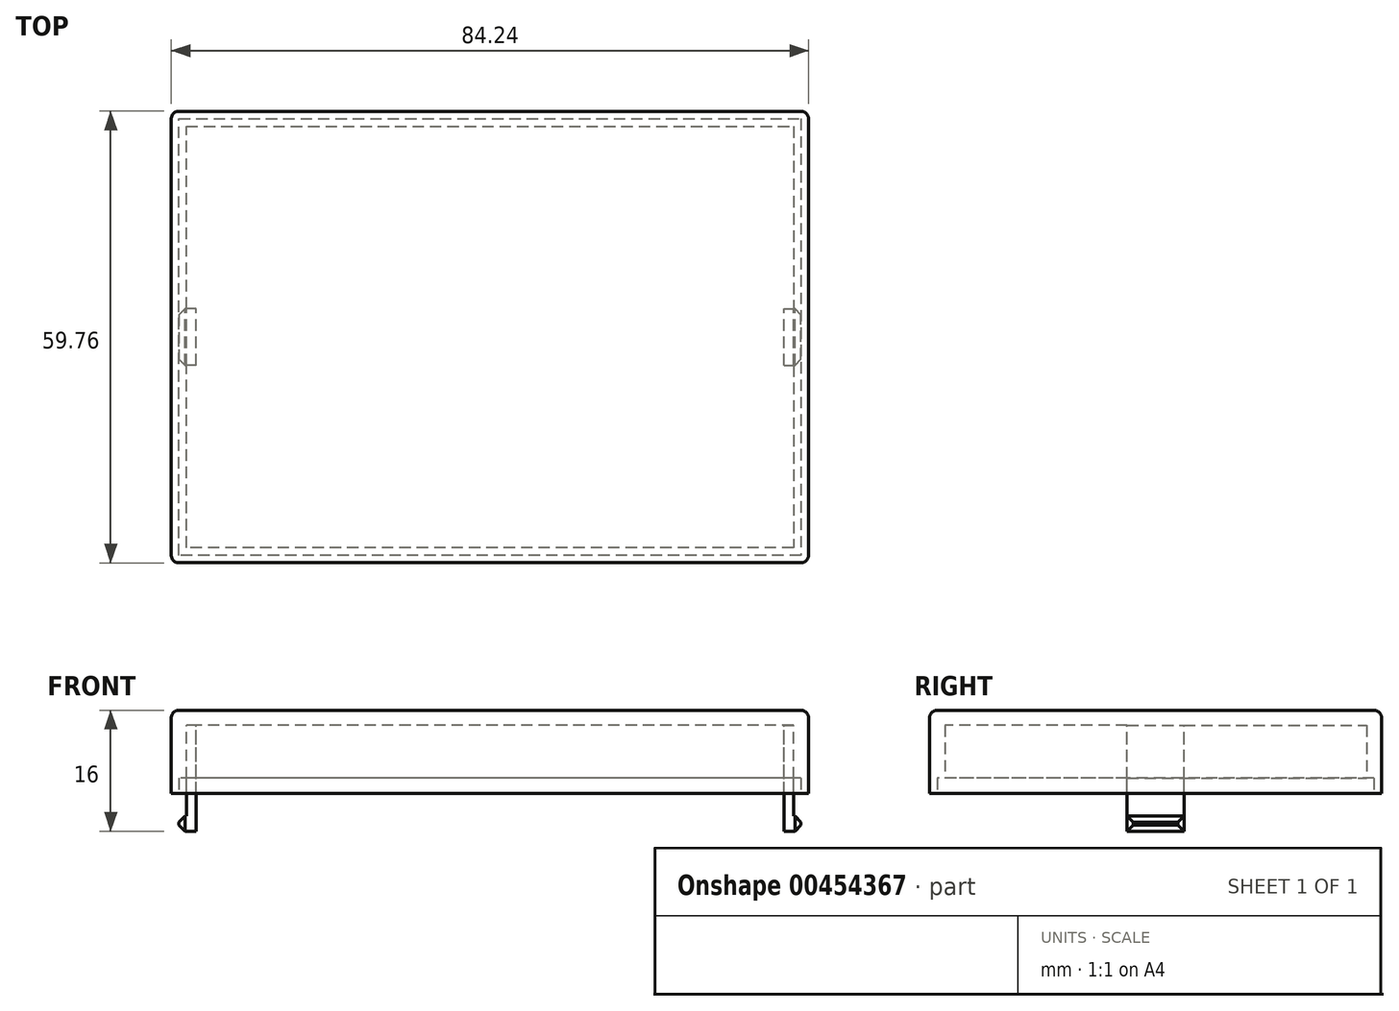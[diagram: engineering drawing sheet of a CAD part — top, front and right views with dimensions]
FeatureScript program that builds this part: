
annotation { "Feature Type Name" : "Feature", "Feature Type Description" : "" }
export const myFeature = defineFeature(function(context is Context, id is Id, definition is map)
    precondition{}
    {
        {
            var Q0;
            Q0=qCreatedBy(makeId("Top.planeOp"),FACE);
            var sketch = newSketch(context, id + "F0", { "sketchPlane" : qUnion([Q0])});
            skLineSegment(sketch, "E0.bottom", {"start": v(42.12, 29.88) * mm, "end": v(-42.12, 29.88) * mm});
            skLineSegment(sketch, "E0.top", {"start": v(42.13, -29.88) * mm, "end": v(-42.12, -29.88) * mm});
            skLineSegment(sketch, "E0.left", {"start": v(42.12, 29.88) * mm, "end": v(42.13, -29.88) * mm});
            skLineSegment(sketch, "E0.right", {"start": v(-42.12, 29.88) * mm, "end": v(-42.12, -29.88) * mm});
            skPoint(sketch, "E0.middle", {"position": v(0, 0) * mm});
            skSolve(sketch);
        }
        {
            var Q0;
            Q0=makeQuery(id+"F0.imprint","IMPRINT",FACE,{"disambiguationData":[TD([[makeQuery(id+"F0.imprint","IMPRINT",EDGE,{"derivedFrom":sQuery(id+"F0.wireOp",EDGE,"E0.bottom")}),1.0]])]});
            extrude(context, id + "F1", {"entities" : qUnion([Q0]), "depth" : 11 * mm});
        }
        {
            var Q0;
            Q0=makeQuery(id+"F1.opExtrude","CAP_FACE",FACE,{"disambiguationData":[OSD([sQuery(id+"F0.wireOp",EDGE,"E0.bottom"),sQuery(id+"F0.wireOp",EDGE,"E0.top"),sQuery(id+"F0.wireOp",EDGE,"E0.left"),sQuery(id+"F0.wireOp",EDGE,"E0.right")])],"isStart":true});
            var sketch = newSketch(context, id + "F2", { "sketchPlane" : qUnion([Q0])});
            skLineSegment(sketch, "E1.0", {"start": v(40.13, 27.88) * mm, "end": v(-40.12, 27.88) * mm});
            skLineSegment(sketch, "E1.1", {"start": v(40.12, -27.88) * mm, "end": v(40.13, 27.88) * mm});
            skLineSegment(sketch, "E1.2", {"start": v(-40.13, -27.88) * mm, "end": v(40.12, -27.88) * mm});
            skLineSegment(sketch, "E1.3", {"start": v(-40.12, 27.88) * mm, "end": v(-40.12, -27.88) * mm});
            skSolve(sketch);
        }
        {
            var Q0;
            Q0=makeQuery(id+"F2.imprint","IMPRINT",FACE,{"disambiguationData":[TD([[makeQuery(id+"F2.imprint","IMPRINT",EDGE,{"derivedFrom":sQuery(id+"F2.wireOp",EDGE,"E1.0")}),1.0]])]});
            extrude(context, id + "F3", {"entities" : qUnion([Q0]), "operationType" : NewBodyOperationType.REMOVE, "oppositeDirection" : true, "depth" : 9 * mm});
        }
        {
            var Q0;
            Q0=makeQuery(id+"F1.opExtrude","CAP_FACE",FACE,{"disambiguationData":[OSD([sQuery(id+"F0.wireOp",EDGE,"E0.bottom"),sQuery(id+"F0.wireOp",EDGE,"E0.top"),sQuery(id+"F0.wireOp",EDGE,"E0.left"),sQuery(id+"F0.wireOp",EDGE,"E0.right")])],"isStart":true});
            var sketch = newSketch(context, id + "F4", { "sketchPlane" : qUnion([Q0])});
            skLineSegment(sketch, "E2.0", {"start": v(41.13, 28.88) * mm, "end": v(-41.12, 28.88) * mm});
            skLineSegment(sketch, "E2.1", {"start": v(41.12, -28.88) * mm, "end": v(41.13, 28.88) * mm});
            skLineSegment(sketch, "E2.2", {"start": v(-41.12, -28.88) * mm, "end": v(41.12, -28.88) * mm});
            skLineSegment(sketch, "E2.3", {"start": v(-41.12, 28.88) * mm, "end": v(-41.12, -28.88) * mm});
            skSolve(sketch);
        }
        {
            var Q0;
            Q0=makeQuery(id+"F4.imprint","IMPRINT",FACE,{"disambiguationData":[TD([[makeQuery(id+"F4.imprint","IMPRINT",EDGE,{"derivedFrom":sQuery(id+"F4.wireOp",EDGE,"E2.0")}),1.0]])]});
            extrude(context, id + "F5", {"entities" : qUnion([Q0]), "operationType" : NewBodyOperationType.REMOVE, "oppositeDirection" : true, "depth" : 2 * mm});
        }
        {
            var Q0;
            Q0=makeQuery(id+"F3.boolean.opBoolean","COPY",FACE,{"derivedFrom":makeQuery(id+"F3.opExtrude","SWEPT_FACE",FACE,{"disambiguationData":[OSD([sQuery(id+"F2.wireOp",EDGE,"E1.3")])]})});
            var sketch = newSketch(context, id + "F6", { "sketchPlane" : qUnion([Q0])});
            skLineSegment(sketch, "E3.bottom", {"start": v(3.75, -5) * mm, "end": v(-3.75, -5) * mm});
            skLineSegment(sketch, "E3.top", {"start": v(3.75, 9) * mm, "end": v(-3.75, 9) * mm});
            skLineSegment(sketch, "E3.left", {"start": v(3.75, -5) * mm, "end": v(3.75, 9) * mm});
            skLineSegment(sketch, "E3.right", {"start": v(-3.75, -5) * mm, "end": v(-3.75, 9) * mm});
            skPoint(sketch, "E3.middle", {"position": v(0, 2) * mm});
            skSolve(sketch);
        }
        {
            var Q0;
            {var subQ0=sQuery(id+"F6.wireOp",EDGE,"E3.bottom");Q0=makeQuery(id+"F6.imprint","IMPRINT",FACE,{"disambiguationData":[TD([[makeQuery(id+"F6.imprint","IMPRINT",EDGE,{"derivedFrom":subQ0}),-1.0]])]});}
            var Q1;
            {var subQ0=sQuery(id+"F6.wireOp",EDGE,"E3.left");var subQ1=sQuery(id+"F2.wireOp",EDGE,"E1.3");var subQ2=makeQuery(id+"F5.boolean.opBoolean","COPY",EDGE,{"derivedFrom":makeQuery(id+"F5.opExtrude","CAP_EDGE",EDGE,{"disambiguationData":[OSD([subQ1])],"isStart":false})});var subQ3=makeQuery(id+"F6.imprint","INTERSECT",VERTEX,{"derivedFrom":[subQ2,subQ0]});Q1=makeQuery(id+"F6.imprint","IMPRINT",FACE,{"disambiguationData":[TD([[makeQuery(id+"F6.imprint","IMPRINT",EDGE,{"disambiguationData":[TD([[subQ3,-1.0]])],"derivedFrom":subQ0}),1.0]])]});}
            extrude(context, id + "F7", {"entities" : qUnion([Q0, Q1]), "operationType" : NewBodyOperationType.ADD, "depth" : 1.25 * mm});
        }
        {
            var Q0;
            Q0=makeQuery(id+"F1.opExtrude","SWEPT_EDGE",EDGE,{"disambiguationData":[OSD([sQuery(id+"F0.wireOp",EDGE,"E0.top"),sQuery(id+"F0.wireOp",EDGE,"E0.right")])]});
            var Q1;
            Q1=makeQuery(id+"F1.opExtrude","SWEPT_EDGE",EDGE,{"disambiguationData":[OSD([sQuery(id+"F0.wireOp",EDGE,"E0.top"),sQuery(id+"F0.wireOp",EDGE,"E0.left")])]});
            var Q2;
            Q2=makeQuery(id+"F1.opExtrude","SWEPT_EDGE",EDGE,{"disambiguationData":[OSD([sQuery(id+"F0.wireOp",EDGE,"E0.bottom"),sQuery(id+"F0.wireOp",EDGE,"E0.right")])]});
            var Q3;
            Q3=makeQuery(id+"F1.opExtrude","SWEPT_EDGE",EDGE,{"disambiguationData":[OSD([sQuery(id+"F0.wireOp",EDGE,"E0.bottom"),sQuery(id+"F0.wireOp",EDGE,"E0.left")])]});
            var Q4;
            Q4=makeQuery(id+"F1.opExtrude","CAP_EDGE",EDGE,{"disambiguationData":[OSD([sQuery(id+"F0.wireOp",EDGE,"E0.bottom")])],"isStart":false});
            var Q5;
            Q5=makeQuery(id+"F1.opExtrude","CAP_EDGE",EDGE,{"disambiguationData":[OSD([sQuery(id+"F0.wireOp",EDGE,"E0.right")])],"isStart":false});
            var Q6;
            Q6=makeQuery(id+"F1.opExtrude","CAP_EDGE",EDGE,{"disambiguationData":[OSD([sQuery(id+"F0.wireOp",EDGE,"E0.top")])],"isStart":false});
            var Q7;
            Q7=makeQuery(id+"F1.opExtrude","CAP_EDGE",EDGE,{"disambiguationData":[OSD([sQuery(id+"F0.wireOp",EDGE,"E0.left")])],"isStart":false});
            fillet(context, id + "F8", {"entities" : qUnion([Q0, Q1, Q2, Q3, Q4, Q5, Q6, Q7]), "radius" : 1 * mm, "tangentPropagation" : true, "allowEdgeOverflow" : false});
        }
        {
            var Q0;
            Q0=makeQuery(id+"F7.opExtrude","CAP_FACE",FACE,{"disambiguationData":[OSD([sQuery(id+"F6.wireOp",EDGE,"E3.bottom"),sQuery(id+"F6.wireOp",EDGE,"E3.top"),sQuery(id+"F6.wireOp",EDGE,"E3.left"),sQuery(id+"F6.wireOp",EDGE,"E3.right")])],"isStart":true});
            var sketch = newSketch(context, id + "F9", { "sketchPlane" : qUnion([Q0])});
            skLineSegment(sketch, "E4.0", {"start": v(-3.75, -3) * mm, "end": v(3.75, -3) * mm});
            skSolve(sketch);
        }
        {
            var Q0;
            {var subQ0=sQuery(id+"F9.wireOp",EDGE,"E4.0");Q0=makeQuery(id+"F9.imprint","IMPRINT",FACE,{"disambiguationData":[TD([[makeQuery(id+"F9.imprint","IMPRINT",EDGE,{"derivedFrom":subQ0}),-1.0]])]});}
            extrude(context, id + "F10", {"entities" : qUnion([Q0]), "operationType" : NewBodyOperationType.ADD, "depth" : 1 * mm});
        }
        {
            var Q0;
            Q0=makeQuery(id+"F10.opExtrude","CAP_FACE",FACE,{"disambiguationData":[OSD([sQuery(id+"F6.wireOp",EDGE,"E3.bottom"),sQuery(id+"F6.wireOp",EDGE,"E3.left"),sQuery(id+"F6.wireOp",EDGE,"E3.right"),sQuery(id+"F9.wireOp",EDGE,"E4.0")])],"isStart":false});
            chamfer(context, id + "F11", {"entities" : qUnion([Q0]), "width" : 0.8 * mm, "tangentPropagation" : true});
        }
        {
            var Q0;
            Q0=makeQuery(id+"F1.opExtrude","SWEPT_BODY",BODY,{"disambiguationData":[OSD([sQuery(id+"F0.wireOp",EDGE,"E0.bottom"),sQuery(id+"F0.wireOp",EDGE,"E0.top"),sQuery(id+"F0.wireOp",EDGE,"E0.left"),sQuery(id+"F0.wireOp",EDGE,"E0.right")])]});
            var Q1;
            Q1=qCreatedBy(makeId("Right.planeOp"),FACE);
            mirror(context, id + "F12", {"operationType" : NewBodyOperationType.ADD, "entities" : qUnion([Q0]), "mirrorPlane" : qUnion([Q1])});
        }
    });
